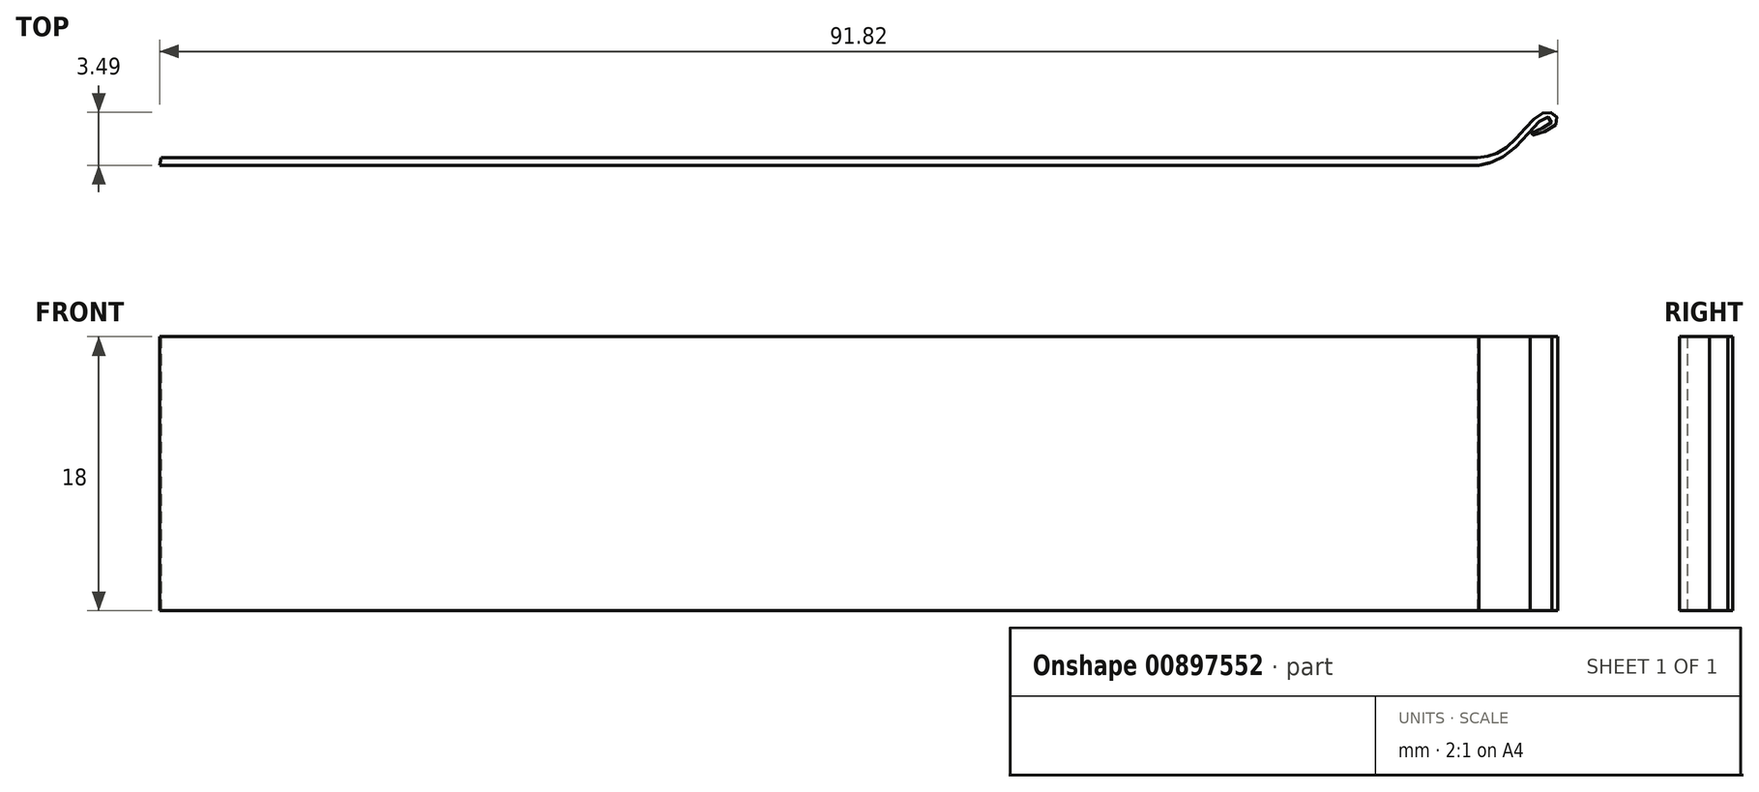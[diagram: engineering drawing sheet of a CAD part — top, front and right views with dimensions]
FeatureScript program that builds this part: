
annotation { "Feature Type Name" : "Feature", "Feature Type Description" : "" }
export const myFeature = defineFeature(function(context is Context, id is Id, definition is map)
    precondition{}
    {
        {
            var Q0;
            Q0=qCreatedBy(makeId("Top.planeOp"),FACE);
            var sketch = newSketch(context, id + "F0", { "sketchPlane" : qUnion([Q0])});
            skLineSegment(sketch, "E0", {"start": v(33.2, 35.56) * mm, "end": v(-53.25, 35.56) * mm});
            skLineSegment(sketch, "E1", {"start": v(33.31, 35.06) * mm, "end": v(-53.33, 35.06) * mm});
            skLineSegment(sketch, "E2", {"start": v(-53.33, 35.06) * mm, "end": v(-53.25, 35.56) * mm});
            skPoint(sketch, "E3", {"position": v(43.33, 38.05) * mm});
            skFitSpline(sketch, "E4", {"points": [v(33.2, 35.56) * mm, v(34.46, 35.83) * mm, v(36, 37.1) * mm, v(37.4, 38.45) * mm, v(38.25, 38.43) * mm, v(38.43, 37.83) * mm, v(36.83, 37.04) * mm, v(36.7, 37.15) * mm, v(38.06, 37.86) * mm, v(37.8, 38.23) * mm, v(35.64, 36.18) * mm, v(34.1, 35.25) * mm, v(33.31, 35.06) * mm], "startDerivative": vector(16.64, 2.9) * mm, "endDerivative": vector(-33.98, -8.76) * mm});
            skSolve(sketch);
        }
        {
            var Q0;
            Q0 = qSketchRegion(id + "F0", true);
            extrude(context, id + "F1", {"entities" : qUnion([Q0]), "depth" : 18 * mm, "offsetDistance" : 25 * mm});
        }
    });
